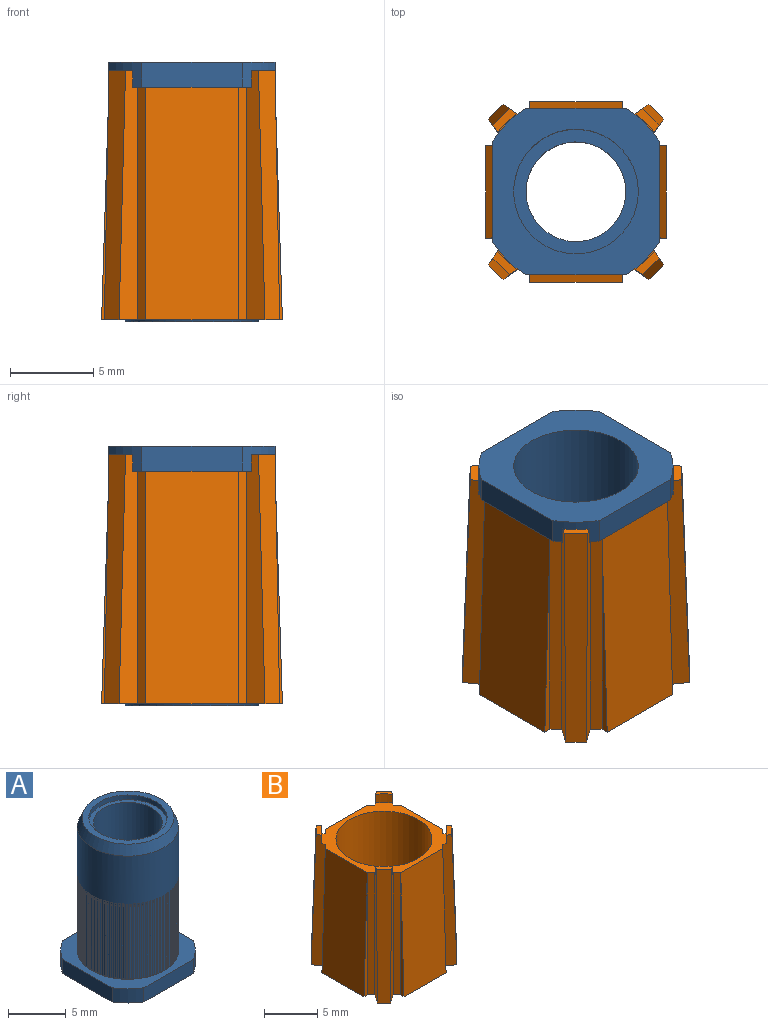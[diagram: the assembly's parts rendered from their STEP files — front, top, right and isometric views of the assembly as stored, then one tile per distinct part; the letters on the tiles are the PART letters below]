
ASSEMBLY  parts=2 mates=1
PART A: 178 faces, bbox 10x10x15.6 mm
  f0: torus R=3.4mm, axis (0,0,1), area 0mm2, adj f1,f171
  f1: cylinder r=0.1mm len=8mm, axis (0,0,-1), area 1.6mm2, adj f0,f162,f171
  f2: torus R=3.4mm, axis (0,0,1), area 0mm2, adj f3,f171
  f3: cylinder r=0.1mm len=8mm, axis (0,0,-1), area 1.6mm2, adj f2,f162,f171
  f4: torus R=3.4mm, axis (0,0,1), area 0mm2, adj f5,f171
  f5: cylinder r=0.1mm len=8mm, axis (0,0,-1), area 1.6mm2, adj f4,f162,f171
  f6: torus R=3.4mm, axis (0,0,1), area 0mm2, adj f7,f171
  f7: cylinder r=0.1mm len=8mm, axis (0,0,-1), area 1.6mm2, adj f6,f162,f171
  f8: torus R=3.4mm, axis (0,0,1), area 0mm2, adj f9,f171
  f9: cylinder r=0.1mm len=8mm, axis (0,0,-1), area 1.6mm2, adj f8,f162,f171
  f10: torus R=3.4mm, axis (0,0,1), area 0mm2, adj f11,f171
  f11: cylinder r=0.1mm len=8mm, axis (0,0,-1), area 1.6mm2, adj f10,f162,f171
  f12: torus R=3.4mm, axis (0,0,1), area 0mm2, adj f13,f171
  f13: cylinder r=0.1mm len=8mm, axis (0,0,-1), area 1.6mm2, adj f12,f162,f171
  f14: torus R=3.4mm, axis (0,0,1), area 0mm2, adj f15,f171
  f15: cylinder r=0.1mm len=8mm, axis (0,0,-1), area 1.6mm2, adj f14,f162,f171
  f16: torus R=3.4mm, axis (0,0,1), area 0mm2, adj f17,f171
  f17: cylinder r=0.1mm len=8mm, axis (0,0,-1), area 1.6mm2, adj f16,f162,f171
  f18: torus R=3.4mm, axis (0,0,1), area 0mm2, adj f19,f171
  f19: cylinder r=0.1mm len=8mm, axis (0,0,-1), area 1.6mm2, adj f18,f162,f171
  f20: torus R=3.4mm, axis (0,0,1), area 0mm2, adj f21,f171
  f21: cylinder r=0.1mm len=8mm, axis (0,0,-1), area 1.6mm2, adj f20,f162,f171
  f22: torus R=3.4mm, axis (0,0,1), area 0mm2, adj f23,f171
  f23: cylinder r=0.1mm len=8mm, axis (0,0,-1), area 1.6mm2, adj f22,f162,f171
  f24: torus R=3.4mm, axis (0,0,1), area 0mm2, adj f25,f171
  f25: cylinder r=0.1mm len=8mm, axis (0,0,-1), area 1.6mm2, adj f24,f162,f171
  f26: torus R=3.4mm, axis (0,0,1), area 0mm2, adj f27,f171
  f27: cylinder r=0.1mm len=8mm, axis (0,0,-1), area 1.6mm2, adj f26,f162,f171
  f28: torus R=3.4mm, axis (0,0,1), area 0mm2, adj f29,f171
  f29: cylinder r=0.1mm len=8mm, axis (0,0,-1), area 1.6mm2, adj f28,f162,f171
  f30: torus R=3.4mm, axis (0,0,1), area 0mm2, adj f31,f171
  f31: cylinder r=0.1mm len=8mm, axis (0,0,-1), area 1.6mm2, adj f30,f162,f171
  f32: torus R=3.4mm, axis (0,0,1), area 0mm2, adj f33,f171
  f33: cylinder r=0.1mm len=8mm, axis (0,0,-1), area 1.6mm2, adj f32,f162,f171
  f34: torus R=3.4mm, axis (0,0,1), area 0mm2, adj f35,f171
  f35: cylinder r=0.1mm len=8mm, axis (0,0,-1), area 1.6mm2, adj f34,f162,f171
  f36: torus R=3.4mm, axis (0,0,1), area 0mm2, adj f37,f171
  f37: cylinder r=0.1mm len=8mm, axis (0,0,-1), area 1.6mm2, adj f36,f162,f171
  f38: torus R=3.4mm, axis (0,0,1), area 0mm2, adj f39,f171
  f39: cylinder r=0.1mm len=8mm, axis (0,0,-1), area 1.6mm2, adj f38,f162,f171
  f40: torus R=3.4mm, axis (0,0,1), area 0mm2, adj f41,f171
  f41: cylinder r=0.1mm len=8mm, axis (0,0,-1), area 1.6mm2, adj f40,f162,f171
  f42: torus R=3.4mm, axis (0,0,1), area 0mm2, adj f43,f171
  f43: cylinder r=0.1mm len=8mm, axis (0,0,-1), area 1.6mm2, adj f42,f162,f171
  f44: torus R=3.4mm, axis (0,0,1), area 0mm2, adj f45,f171
  f45: cylinder r=0.1mm len=8mm, axis (0,0,-1), area 1.6mm2, adj f44,f162,f171
  f46: torus R=3.4mm, axis (0,0,1), area 0mm2, adj f47,f171
  f47: cylinder r=0.1mm len=8mm, axis (0,0,-1), area 1.6mm2, adj f46,f162,f171
  f48: torus R=3.4mm, axis (0,0,1), area 0mm2, adj f49,f171
  f49: cylinder r=0.1mm len=8mm, axis (0,0,-1), area 1.6mm2, adj f48,f162,f171
  f50: torus R=3.4mm, axis (0,0,1), area 0mm2, adj f51,f171
  f51: cylinder r=0.1mm len=8mm, axis (0,0,-1), area 1.6mm2, adj f50,f162,f171
  f52: torus R=3.4mm, axis (0,0,1), area 0mm2, adj f53,f171
  f53: cylinder r=0.1mm len=8mm, axis (0,0,-1), area 1.6mm2, adj f52,f162,f171
  f54: torus R=3.4mm, axis (0,0,1), area 0mm2, adj f55,f171
  f55: cylinder r=0.1mm len=8mm, axis (0,0,-1), area 1.6mm2, adj f54,f162,f171
  f56: torus R=3.4mm, axis (0,0,1), area 0mm2, adj f57,f171
  f57: cylinder r=0.1mm len=8mm, axis (0,0,-1), area 1.6mm2, adj f56,f162,f171
  f58: torus R=3.4mm, axis (0,0,1), area 0mm2, adj f59,f171
  f59: cylinder r=0.1mm len=8mm, axis (0,0,-1), area 1.6mm2, adj f58,f162,f171
  f60: torus R=3.4mm, axis (0,0,1), area 0mm2, adj f61,f171
  f61: cylinder r=0.1mm len=8mm, axis (0,0,-1), area 1.6mm2, adj f60,f162,f171
  f62: torus R=3.4mm, axis (0,0,1), area 0mm2, adj f63,f171
  f63: cylinder r=0.1mm len=8mm, axis (0,0,-1), area 1.6mm2, adj f62,f162,f171
  f64: torus R=3.4mm, axis (0,0,1), area 0mm2, adj f65,f171
  f65: cylinder r=0.1mm len=8mm, axis (0,0,-1), area 1.6mm2, adj f64,f162,f171
  f66: torus R=3.4mm, axis (0,0,1), area 0mm2, adj f67,f171
  f67: cylinder r=0.1mm len=8mm, axis (0,0,-1), area 1.6mm2, adj f66,f162,f171
  f68: torus R=3.4mm, axis (0,0,1), area 0mm2, adj f69,f171
  f69: cylinder r=0.1mm len=8mm, axis (0,0,-1), area 1.6mm2, adj f68,f162,f171
  f70: torus R=3.4mm, axis (0,0,1), area 0mm2, adj f71,f171
  f71: cylinder r=0.1mm len=8mm, axis (0,0,-1), area 1.6mm2, adj f70,f162,f171
  f72: torus R=3.4mm, axis (0,0,1), area 0mm2, adj f73,f171
  f73: cylinder r=0.1mm len=8mm, axis (0,0,-1), area 1.6mm2, adj f72,f162,f171
  f74: torus R=3.4mm, axis (0,0,1), area 0mm2, adj f75,f171
  f75: cylinder r=0.1mm len=8mm, axis (0,0,-1), area 1.6mm2, adj f74,f162,f171
  f76: torus R=3.4mm, axis (0,0,1), area 0mm2, adj f77,f171
  f77: cylinder r=0.1mm len=8mm, axis (0,0,-1), area 1.6mm2, adj f76,f162,f171
  f78: torus R=3.4mm, axis (0,0,1), area 0mm2, adj f79,f171
  f79: cylinder r=0.1mm len=8mm, axis (0,0,-1), area 1.6mm2, adj f78,f162,f171
  f80: torus R=3.4mm, axis (0,0,1), area 0mm2, adj f81,f171
  f81: cylinder r=0.1mm len=8mm, axis (0,0,-1), area 1.6mm2, adj f80,f162,f171
  f82: torus R=3.4mm, axis (0,0,1), area 0mm2, adj f83,f171
  f83: cylinder r=0.1mm len=8mm, axis (0,0,-1), area 1.6mm2, adj f82,f162,f171
  f84: torus R=3.4mm, axis (0,0,1), area 0mm2, adj f85,f171
  f85: cylinder r=0.1mm len=8mm, axis (0,0,-1), area 1.6mm2, adj f84,f162,f171
  f86: torus R=3.4mm, axis (0,0,1), area 0mm2, adj f87,f171
  f87: cylinder r=0.1mm len=8mm, axis (0,0,-1), area 1.6mm2, adj f86,f162,f171
  f88: torus R=3.4mm, axis (0,0,1), area 0mm2, adj f89,f171
  f89: cylinder r=0.1mm len=8mm, axis (0,0,-1), area 1.6mm2, adj f88,f162,f171
  f90: torus R=3.4mm, axis (0,0,1), area 0mm2, adj f91,f171
  f91: cylinder r=0.1mm len=8mm, axis (0,0,-1), area 1.6mm2, adj f90,f162,f171
  f92: torus R=3.4mm, axis (0,0,1), area 0mm2, adj f93,f171
  f93: cylinder r=0.1mm len=8mm, axis (0,0,-1), area 1.6mm2, adj f92,f162,f171
  f94: torus R=3.4mm, axis (0,0,1), area 0mm2, adj f95,f171
  f95: cylinder r=0.1mm len=8mm, axis (0,0,-1), area 1.6mm2, adj f94,f162,f171
  f96: torus R=3.4mm, axis (0,0,1), area 0mm2, adj f97,f171
  f97: cylinder r=0.1mm len=8mm, axis (0,0,-1), area 1.6mm2, adj f96,f162,f171
  f98: torus R=3.4mm, axis (0,0,1), area 0mm2, adj f99,f171
  f99: cylinder r=0.1mm len=8mm, axis (0,0,-1), area 1.6mm2, adj f98,f162,f171
  f100: torus R=3.4mm, axis (0,0,1), area 0mm2, adj f101,f171
  f101: cylinder r=0.1mm len=8mm, axis (0,0,-1), area 1.6mm2, adj f100,f162,f171
  f102: torus R=3.4mm, axis (0,0,1), area 0mm2, adj f103,f171
  f103: cylinder r=0.1mm len=8mm, axis (0,0,-1), area 1.6mm2, adj f102,f162,f171
  f104: torus R=3.4mm, axis (0,0,1), area 0mm2, adj f105,f171
  f105: cylinder r=0.1mm len=8mm, axis (0,0,-1), area 1.6mm2, adj f104,f162,f171
  f106: torus R=3.4mm, axis (0,0,1), area 0mm2, adj f107,f171
  f107: cylinder r=0.1mm len=8mm, axis (0,0,-1), area 1.6mm2, adj f106,f162,f171
  f108: torus R=3.4mm, axis (0,0,1), area 0mm2, adj f109,f171
  f109: cylinder r=0.1mm len=8mm, axis (0,0,-1), area 1.6mm2, adj f108,f162,f171
  f110: torus R=3.4mm, axis (0,0,1), area 0mm2, adj f111,f171
  f111: cylinder r=0.1mm len=8mm, axis (0,0,-1), area 1.6mm2, adj f110,f162,f171
  f112: torus R=3.4mm, axis (0,0,1), area 0mm2, adj f113,f171
  f113: cylinder r=0.1mm len=8mm, axis (0,0,-1), area 1.6mm2, adj f112,f162,f171
  f114: torus R=3.4mm, axis (0,0,1), area 0mm2, adj f115,f171
  f115: cylinder r=0.1mm len=8mm, axis (0,0,-1), area 1.6mm2, adj f114,f162,f171
  f116: torus R=3.4mm, axis (0,0,1), area 0mm2, adj f117,f171
  f117: cylinder r=0.1mm len=8mm, axis (0,0,-1), area 1.6mm2, adj f116,f162,f171
  f118: torus R=3.4mm, axis (0,0,1), area 0mm2, adj f119,f171
  f119: cylinder r=0.1mm len=8mm, axis (0,0,-1), area 1.6mm2, adj f118,f162,f171
  f120: torus R=3.4mm, axis (0,0,1), area 0mm2, adj f121,f171
  f121: cylinder r=0.1mm len=8mm, axis (0,0,-1), area 1.6mm2, adj f120,f162,f171
  f122: torus R=3.4mm, axis (0,0,1), area 0mm2, adj f123,f171
  f123: cylinder r=0.1mm len=8mm, axis (0,0,-1), area 1.6mm2, adj f122,f162,f171
  f124: torus R=3.4mm, axis (0,0,1), area 0mm2, adj f125,f171
  f125: cylinder r=0.1mm len=8mm, axis (0,0,-1), area 1.6mm2, adj f124,f162,f171
  f126: torus R=3.4mm, axis (0,0,1), area 0mm2, adj f127,f171
  f127: cylinder r=0.1mm len=8mm, axis (0,0,-1), area 1.6mm2, adj f126,f162,f171
  f128: torus R=3.4mm, axis (0,0,1), area 0mm2, adj f129,f171
  f129: cylinder r=0.1mm len=8mm, axis (0,0,-1), area 1.6mm2, adj f128,f162,f171
  f130: torus R=3.4mm, axis (0,0,1), area 0mm2, adj f131,f171
  f131: cylinder r=0.1mm len=8mm, axis (0,0,-1), area 1.6mm2, adj f130,f162,f171
  f132: torus R=3.4mm, axis (0,0,1), area 0mm2, adj f133,f171
  f133: cylinder r=0.1mm len=8mm, axis (0,0,-1), area 1.6mm2, adj f132,f162,f171
  f134: torus R=3.4mm, axis (0,0,1), area 0mm2, adj f135,f171
  f135: cylinder r=0.1mm len=8mm, axis (0,0,-1), area 1.6mm2, adj f134,f162,f171
  f136: torus R=3.4mm, axis (0,0,1), area 0mm2, adj f137,f171
  f137: cylinder r=0.1mm len=8mm, axis (0,0,-1), area 1.6mm2, adj f136,f162,f171
  f138: torus R=3.4mm, axis (0,0,1), area 0mm2, adj f139,f171
  f139: cylinder r=0.1mm len=8mm, axis (0,0,-1), area 1.6mm2, adj f138,f162,f171
  f140: torus R=3.4mm, axis (0,0,1), area 0mm2, adj f141,f171
  f141: cylinder r=0.1mm len=8mm, axis (0,0,-1), area 1.6mm2, adj f140,f162,f171
  f142: torus R=3.4mm, axis (0,0,1), area 0mm2, adj f143,f171
  f143: cylinder r=0.1mm len=8mm, axis (0,0,-1), area 1.6mm2, adj f142,f162,f171
  f144: torus R=3.4mm, axis (0,0,1), area 0mm2, adj f145,f171
  f145: cylinder r=0.1mm len=8mm, axis (0,0,-1), area 1.6mm2, adj f144,f162,f171
  f146: torus R=3.4mm, axis (0,0,1), area 0mm2, adj f147,f171
  f147: cylinder r=0.1mm len=8mm, axis (0,0,-1), area 1.6mm2, adj f146,f162,f171
  f148: torus R=3.4mm, axis (0,0,1), area 0mm2, adj f149,f171
  f149: cylinder r=0.1mm len=8mm, axis (0,0,-1), area 1.6mm2, adj f148,f162,f171
  f150: torus R=3.4mm, axis (0,0,1), area 0mm2, adj f151,f171
  f151: cylinder r=0.1mm len=8mm, axis (0,0,-1), area 1.6mm2, adj f150,f162,f171
  f152: torus R=3.4mm, axis (0,0,1), area 0mm2, adj f153,f171
  f153: cylinder r=0.1mm len=8mm, axis (0,0,-1), area 1.6mm2, adj f152,f162,f171
  f154: torus R=3.4mm, axis (0,0,1), area 0mm2, adj f155,f171
  f155: cylinder r=0.1mm len=8mm, axis (0,0,-1), area 1.6mm2, adj f154,f162,f171
  f156: torus R=3.4mm, axis (0,0,1), area 0mm2, adj f157,f171
  f157: cylinder r=0.1mm len=8mm, axis (0,0,-1), area 1.6mm2, adj f156,f162,f171
  f158: plane 10x10mm, normal (0,0,-1), area 49.4mm2, adj f159,f160,f161,f169,f170,f172,f173,f174
  f159: cylinder r=5.85mm len=1.96mm, axis (0,0,-1), area 4.2mm2, adj f158,f162,f174,f175
  f160: cylinder r=5.85mm len=1.96mm, axis (0,0,-1), area 4.2mm2, adj f158,f162,f172,f174
  f161: cylinder r=5.85mm len=1.96mm, axis (0,0,-1), area 4.2mm2, adj f158,f162,f173,f175
  f162: plane 10x10mm, normal (0,0,1), area 33.2mm2, adj f1,f3,f5,f7,f9,f11,f13,f15
  f163: cone r=4mm half-angle=21.8deg, axis (0,0,-1), area 28.4mm2, adj f164,f171
  f164: plane 8x8mm, normal (0,0,1), area 13.9mm2, adj f163,f165
  f165: cylinder r=3.4mm len=6.8mm, axis (0,0,-1), area 10.7mm2, adj f164,f166
  f166: plane 6.8x6.8mm, normal (0,0,1), area 8mm2, adj f165,f167
  f167: cylinder r=3mm len=7.6mm, axis (0,0,-1), area 143.3mm2, adj f166,f168
  f168: plane 7.5x7.5mm, normal (0,0,-1), area 15.9mm2, adj f167,f169
  f169: cylinder r=3.75mm len=7.5mm, axis (0,0,-1), area 176.7mm2, adj f158,f168
  f170: cylinder r=5.85mm len=1.96mm, axis (0,0,-1), area 4.2mm2, adj f158,f162,f172,f173
  f171: cylinder r=4.4mm len=13.1mm, axis (0,0,-1), area 251.6mm2, adj f0,f1,f2,f3,f4,f5,f6,f7
  f172: plane 6.07x1.5mm, normal (0,1,0), area 9.1mm2, adj f158,f160,f162,f170
  f173: plane 6.07x1.5mm, normal (-1,0,0), area 9.1mm2, adj f158,f161,f162,f170
  f174: plane 6.07x1.5mm, normal (1,0,0), area 9.1mm2, adj f158,f159,f160,f162
  f175: plane 6.07x1.5mm, normal (0,-1,0), area 9.1mm2, adj f158,f159,f161,f162
  f176: cylinder r=0.1mm len=8mm, axis (0,0,-1), area 1.6mm2, adj f162,f171,f177
  f177: torus R=3.4mm, axis (0,0,1), area 0mm2, adj f171,f176
PART B: 43 faces, bbox 10.9x10.9x15 mm
  f0: plane 10x10mm, normal (0,0,1), area 29.1mm2, adj f2,f4,f5,f6,f7,f8,f9,f10
  f1: plane 10.88x10.88mm, normal (0,0,-1), area 44.3mm2, adj f2,f3,f4,f5,f6,f7,f8,f9
  f2: cylinder r=4.5mm len=14mm, axis (0,0,-1), area 395.8mm2, adj f0,f1
  f3: plane 15x1.27mm, normal (-0.71,-0.71,0.03), area 20mm2, adj f1,f4,f7,f25
  f4: plane 15x1.11mm, normal (-0.82,0.57,0), area 16.3mm2, adj f0,f1,f3,f5,f24,f25
  f5: plane 14x0.5mm, normal (-0.71,-0.71,0), area 9.9mm2, adj f0,f1,f4,f33
  f6: plane 14x0.5mm, normal (-0.71,-0.71,0), area 9.9mm2, adj f0,f1,f7,f30
  f7: plane 15x1.11mm, normal (0.57,-0.82,0), area 16.3mm2, adj f0,f1,f3,f6,f24,f25
  f8: plane 15x1.11mm, normal (-0.57,-0.82,0), area 16.3mm2, adj f0,f1,f9,f26,f27,f42
  f9: plane 14x0.5mm, normal (0.71,-0.71,0), area 9.9mm2, adj f0,f1,f8,f28
  f10: plane 14x0.5mm, normal (0.71,-0.71,0), area 9.9mm2, adj f0,f1,f11,f36
  f11: plane 15x1.11mm, normal (0.82,0.57,0), area 16.3mm2, adj f0,f1,f10,f26,f27,f42
  f12: plane 15x1.11mm, normal (0.82,-0.57,0), area 16.3mm2, adj f0,f1,f13,f20,f21,f41
  f13: plane 14x0.5mm, normal (0.71,0.71,0), area 9.9mm2, adj f0,f1,f12,f35
  f14: plane 14x0.5mm, normal (0.71,0.71,0), area 9.9mm2, adj f0,f1,f15,f39
  f15: plane 15x1.11mm, normal (-0.57,0.82,0), area 16.3mm2, adj f0,f1,f14,f20,f21,f41
  f16: plane 15x1.11mm, normal (0.57,0.82,0), area 16.3mm2, adj f0,f1,f17,f22,f23,f40
  f17: plane 14x0.5mm, normal (-0.71,0.71,0), area 9.9mm2, adj f0,f1,f16,f38
  f18: plane 14x0.5mm, normal (-0.71,0.71,0), area 9.9mm2, adj f0,f1,f19,f32
  f19: plane 15x1.11mm, normal (-0.82,-0.57,0), area 16.3mm2, adj f0,f1,f18,f22,f23,f40
  f20: cylinder r=5.9mm len=1.13mm, axis (0,0,-1), area 1.6mm2, adj f0,f12,f15,f21
  f21: plane 1.43x1.43mm, normal (0,0,1), area 0.7mm2, adj f12,f15,f20,f41
  f22: cylinder r=5.9mm len=1.13mm, axis (0,0,-1), area 1.6mm2, adj f0,f16,f19,f23
  f23: plane 1.43x1.43mm, normal (0,0,1), area 0.7mm2, adj f16,f19,f22,f40
  f24: cylinder r=5.9mm len=1.13mm, axis (0,0,-1), area 1.6mm2, adj f0,f4,f7,f25
  f25: plane 1.43x1.43mm, normal (0,0,1), area 0.7mm2, adj f3,f4,f7,f24
  f26: cylinder r=5.9mm len=1.13mm, axis (0,0,-1), area 1.6mm2, adj f0,f8,f11,f27
  f27: plane 1.43x1.43mm, normal (0,0,1), area 0.7mm2, adj f8,f11,f26,f42
  f28: plane 14x0.44mm, normal (1,0,0), area 3.1mm2, adj f1,f9,f29
  f29: plane 14x5.57mm, normal (0,-1,0.03), area 78mm2, adj f0,f1,f28,f30
  f30: plane 14x0.44mm, normal (-1,0,0), area 3.1mm2, adj f1,f6,f29
  f31: plane 14x5.57mm, normal (-1,0,0.03), area 78mm2, adj f0,f1,f32,f33
  f32: plane 14x0.44mm, normal (0,1,0), area 3.1mm2, adj f1,f18,f31
  f33: plane 14x0.44mm, normal (0,-1,0), area 3.1mm2, adj f1,f5,f31
  f34: plane 14x5.57mm, normal (1,0,0.03), area 78mm2, adj f0,f1,f35,f36
  f35: plane 14x0.44mm, normal (0,1,0), area 3.1mm2, adj f1,f13,f34
  f36: plane 14x0.44mm, normal (0,-1,0), area 3.1mm2, adj f1,f10,f34
  f37: plane 14x5.57mm, normal (0,1,0.03), area 78mm2, adj f0,f1,f38,f39
  f38: plane 14x0.44mm, normal (-1,0,0), area 3.1mm2, adj f1,f17,f37
  f39: plane 14x0.44mm, normal (1,0,0), area 3.1mm2, adj f1,f14,f37
  f40: plane 15x1.27mm, normal (-0.71,0.71,0.03), area 20mm2, adj f1,f16,f19,f23
  f41: plane 15x1.27mm, normal (0.71,0.71,0.03), area 20mm2, adj f1,f12,f15,f21
  f42: plane 15x1.27mm, normal (0.71,-0.71,0.03), area 20mm2, adj f1,f8,f11,f27
PLACE A rot(axis=(0,1,0),180deg) t=(0,0,15.5)mm
PLACE B at identity fixed
MATE fastened B.f2 <-> A.f0  axis (0,0,-1) through (0,0,14)mm
